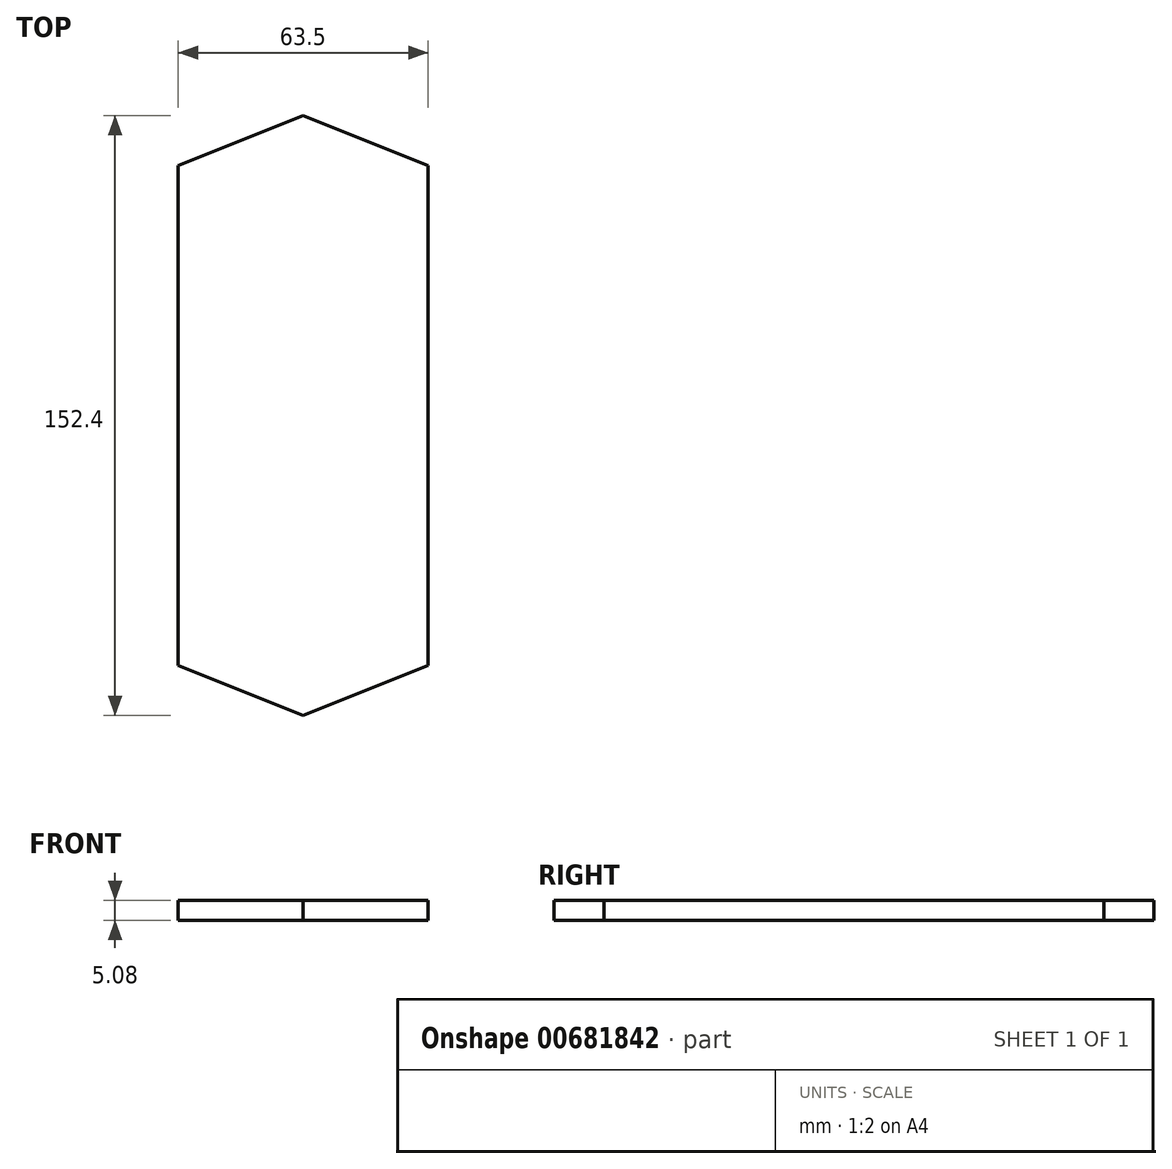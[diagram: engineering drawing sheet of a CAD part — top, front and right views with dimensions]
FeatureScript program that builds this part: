
annotation { "Feature Type Name" : "Feature", "Feature Type Description" : "" }
export const myFeature = defineFeature(function(context is Context, id is Id, definition is map)
    precondition{}
    {
        {
            var Q0;
            Q0=qCreatedBy(makeId("Top.planeOp"),FACE);
            var sketch = newSketch(context, id + "F0", { "sketchPlane" : qUnion([Q0])});
            skLineSegment(sketch, "E0.bottom", {"start": v(0, 0) * mm, "end": v(-63.5, 0) * mm});
            skLineSegment(sketch, "E0.top", {"start": v(0, 127) * mm, "end": v(-63.5, 127) * mm, "construction": true});
            skLineSegment(sketch, "E0.left", {"start": v(0, 0) * mm, "end": v(0, 127) * mm});
            skLineSegment(sketch, "E0.right", {"start": v(-63.5, 0) * mm, "end": v(-63.5, 127) * mm});
            skLineSegment(sketch, "E1", {"start": v(-63.5, 127) * mm, "end": v(-31.75, 139.7) * mm});
            skLineSegment(sketch, "E2", {"start": v(-31.75, 139.7) * mm, "end": v(0, 127) * mm});
            skLineSegment(sketch, "E3", {"start": v(-63.5, 0) * mm, "end": v(-31.75, -12.7) * mm});
            skLineSegment(sketch, "E4", {"start": v(-31.75, -12.7) * mm, "end": v(0, 0) * mm});
            skSolve(sketch);
        }
        {
            var Q0;
            Q0 = qSketchRegion(id + "F0", true);
            extrude(context, id + "F1", {"entities" : qUnion([Q0]), "depth" : 5.08 * mm, "offsetDistance" : 25.4 * mm});
        }
        {
            var Q0;
            Q0=makeQuery(id+"F1.opExtrude","CAP_FACE",FACE,{"disambiguationData":[OSD([sQuery(id+"F0.wireOp",EDGE,"E0.left"),sQuery(id+"F0.wireOp",EDGE,"E0.right"),sQuery(id+"F0.wireOp",EDGE,"E1"),sQuery(id+"F0.wireOp",EDGE,"E2"),sQuery(id+"F0.wireOp",EDGE,"E3"),sQuery(id+"F0.wireOp",EDGE,"E4")])],"isStart":false});
            cPlane(context, id + "F2", {"entities" : qUnion([Q0]), "cplaneType" : CPlaneType.OFFSET, "offset" : 25.4 * mm, "width" : 152.4 * mm, "height" : 152.4 * mm});
        }
    });
